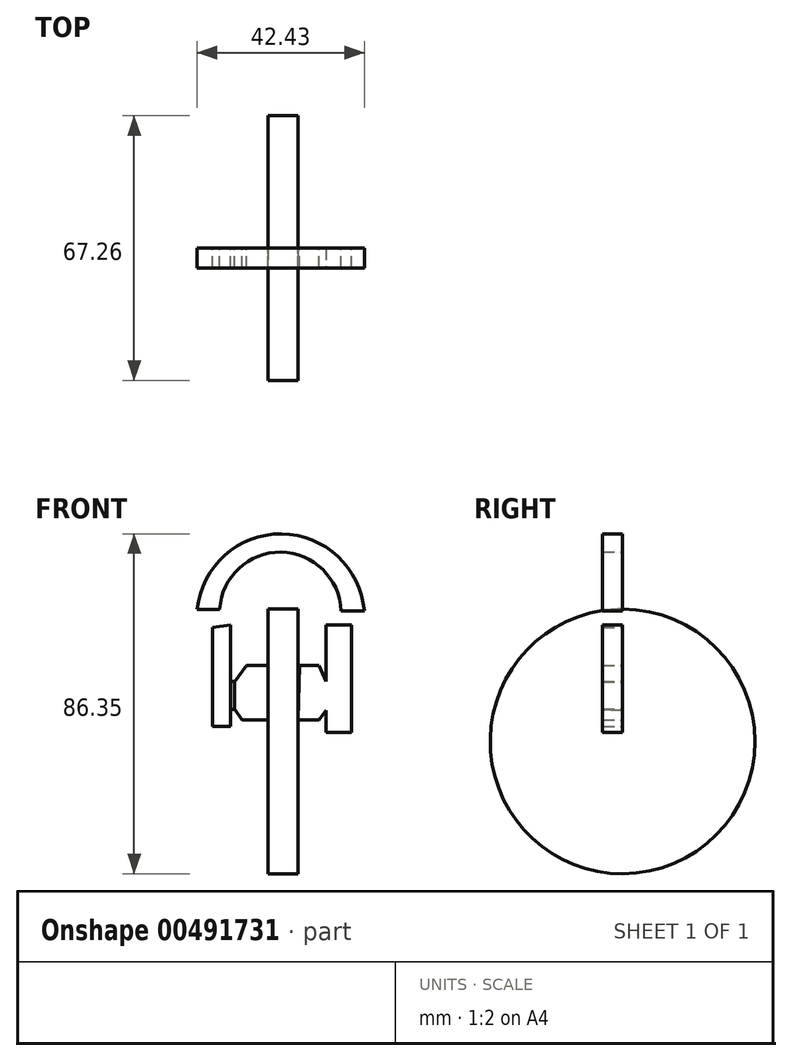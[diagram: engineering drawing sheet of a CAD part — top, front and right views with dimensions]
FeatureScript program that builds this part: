
annotation { "Feature Type Name" : "Feature", "Feature Type Description" : "" }
export const myFeature = defineFeature(function(context is Context, id is Id, definition is map)
    precondition{}
    {
        {
            var Q0;
            Q0=qCreatedBy(makeId("Right.planeOp"),FACE);
            var sketch = newSketch(context, id + "F0", { "sketchPlane" : qUnion([Q0])});
            skCircle(sketch, "E0", {"center": v(0, 0) * mm, "radius": 33.63 * mm});
            skLineSegment(sketch, "E1", {"start": v(-0.53, 0) * mm, "end": v(14.39, 30.4) * mm});
            skLineSegment(sketch, "E2", {"start": v(0.76, 0) * mm, "end": v(15.27, 29.96) * mm});
            skLineSegment(sketch, "E3", {"start": v(15.27, 29.96) * mm, "end": v(14.39, 30.4) * mm});
            skLineSegment(sketch, "E4", {"start": v(0.76, 0) * mm, "end": v(-0.53, 0) * mm});
            skSolve(sketch);
        }
        {
            var Q0;
            Q0 = qSketchRegion(id + "F0", true);
            extrude(context, id + "F1", {"entities" : qUnion([Q0]), "depth" : 7.62 * mm});
        }
        {
            var Q0;
            Q0=qCreatedBy(makeId("Front.planeOp"),FACE);
            var sketch = newSketch(context, id + "F2", { "sketchPlane" : qUnion([Q0])});
            skLineSegment(sketch, "E5", {"start": v(8.1, 19.35) * mm, "end": v(12.93, 19.35) * mm});
            skLineSegment(sketch, "E6", {"start": v(12.93, 19.35) * mm, "end": v(14.82, 15.14) * mm});
            skLineSegment(sketch, "E7", {"start": v(14.82, 15.14) * mm, "end": v(14.82, 8) * mm});
            skLineSegment(sketch, "E8", {"start": v(14.82, 8) * mm, "end": v(12.93, 5.47) * mm});
            skLineSegment(sketch, "E9", {"start": v(12.93, 5.47) * mm, "end": v(7.68, 5.47) * mm});
            skLineSegment(sketch, "E10", {"start": v(7.68, 5.47) * mm, "end": v(8.1, 19.35) * mm});
            skLineSegment(sketch, "E11", {"start": v(0, 19.35) * mm, "end": v(-5.36, 19.35) * mm});
            skLineSegment(sketch, "E12", {"start": v(-5.36, 19.35) * mm, "end": v(-8.52, 15.14) * mm});
            skLineSegment(sketch, "E13", {"start": v(-8.52, 15.14) * mm, "end": v(-8.52, 8.2) * mm});
            skLineSegment(sketch, "E14", {"start": v(-8.52, 8.2) * mm, "end": v(-6.62, 5.47) * mm});
            skLineSegment(sketch, "E15", {"start": v(-6.62, 5.47) * mm, "end": v(0, 5.47) * mm});
            skLineSegment(sketch, "E16", {"start": v(0, 5.47) * mm, "end": v(0, 19.35) * mm});
            skSolve(sketch);
        }
        {
            var Q0;
            Q0=makeQuery(id+"F2.imprint","IMPRINT",FACE,{"disambiguationData":[TD([[makeQuery(id+"F2.imprint","IMPRINT",EDGE,{"derivedFrom":sQuery(id+"F2.wireOp",EDGE,"E5")}),-1.0]])]});
            var Q1;
            Q1=makeQuery(id+"F2.imprint","IMPRINT",FACE,{"disambiguationData":[TD([[makeQuery(id+"F2.imprint","IMPRINT",EDGE,{"derivedFrom":sQuery(id+"F2.wireOp",EDGE,"E11")}),1.0]])]});
            extrude(context, id + "F3", {"entities" : qUnion([Q0, Q1]), "operationType" : NewBodyOperationType.ADD, "depth" : 5.08 * mm});
        }
        {
            var Q0;
            Q0=qCreatedBy(makeId("Front.planeOp"),FACE);
            var sketch = newSketch(context, id + "F4", { "sketchPlane" : qUnion([Q0])});
            skArc(sketch, "E17", {"start": v(24.49, 33.14) * mm, "mid": v(3.46, 52.72) * mm, "end": v(-17.94, 33.57) * mm});
            skLineSegment(sketch, "E18", {"start": v(-17.94, 33.57) * mm, "end": v(-12.24, 33.57) * mm});
            skLineSegment(sketch, "E19", {"start": v(-12.24, 33.57) * mm, "end": v(-17.94, 33.57) * mm});
            skLineSegment(sketch, "E20", {"start": v(24.49, 33.14) * mm, "end": v(18.58, 33.14) * mm});
            skLineSegment(sketch, "E21", {"start": v(18.58, 33.14) * mm, "end": v(24.49, 33.14) * mm});
            skArc(sketch, "E22", {"start": v(18.58, 33.14) * mm, "mid": v(3.37, 48.09) * mm, "end": v(-12.24, 33.57) * mm});
            skLineSegment(sketch, "E23", {"start": v(-12.24, 33.57) * mm, "end": v(-9.5, 29.56) * mm});
            skLineSegment(sketch, "E24", {"start": v(-9.5, 29.56) * mm, "end": v(-12.24, 33.57) * mm});
            skLineSegment(sketch, "E25", {"start": v(-17.94, 33.57) * mm, "end": v(-14, 28.98) * mm});
            skLineSegment(sketch, "E26", {"start": v(-14, 28.98) * mm, "end": v(-9.5, 29.56) * mm});
            skLineSegment(sketch, "E27", {"start": v(18.58, 33.14) * mm, "end": v(14.78, 29.56) * mm});
            skLineSegment(sketch, "E28", {"start": v(14.78, 29.56) * mm, "end": v(18.58, 33.14) * mm});
            skLineSegment(sketch, "E29", {"start": v(24.49, 33.14) * mm, "end": v(21.21, 29.56) * mm});
            skLineSegment(sketch, "E30", {"start": v(21.21, 29.56) * mm, "end": v(14.78, 29.56) * mm});
            skLineSegment(sketch, "E31", {"start": v(-14, 28.98) * mm, "end": v(-14, 3.8) * mm});
            skLineSegment(sketch, "E32", {"start": v(-14, 3.8) * mm, "end": v(-9.5, 3.8) * mm});
            skLineSegment(sketch, "E33", {"start": v(-9.5, 3.8) * mm, "end": v(-9.5, 29.56) * mm});
            skLineSegment(sketch, "E34", {"start": v(14.78, 29.56) * mm, "end": v(14.78, 2.32) * mm});
            skLineSegment(sketch, "E35", {"start": v(14.78, 2.32) * mm, "end": v(21.21, 2.32) * mm});
            skLineSegment(sketch, "E36", {"start": v(21.21, 2.32) * mm, "end": v(21.21, 29.56) * mm});
            skLineSegment(sketch, "E37", {"start": v(-9.5, 15.24) * mm, "end": v(-8.44, 15.24) * mm});
            skLineSegment(sketch, "E38", {"start": v(-8.44, 15.24) * mm, "end": v(-8.44, 8.14) * mm});
            skLineSegment(sketch, "E39", {"start": v(-8.44, 8.14) * mm, "end": v(-9.5, 8.14) * mm});
            skLineSegment(sketch, "E40", {"start": v(-9.5, 8.14) * mm, "end": v(-9.5, 15.24) * mm});
            skSolve(sketch);
        }
        {
            var Q0;
            Q0=makeQuery(id+"F4.imprint","IMPRINT",FACE,{"disambiguationData":[TD([[makeQuery(id+"F4.imprint","IMPRINT",EDGE,{"derivedFrom":sQuery(id+"F4.wireOp",EDGE,"E17")}),1.0]])]});
            var Q1;
            {var subQ3=sQuery(id+"F4.wireOp",EDGE,"E26");Q1=makeQuery(id+"F4.imprint","IMPRINT",FACE,{"disambiguationData":[TD([[makeQuery(id+"F4.imprint","IMPRINT",EDGE,{"derivedFrom":subQ3}),-1.0]])]});}
            var Q2;
            Q2=makeQuery(id+"F4.imprint","IMPRINT",FACE,{"disambiguationData":[TD([[makeQuery(id+"F4.imprint","IMPRINT",EDGE,{"derivedFrom":sQuery(id+"F4.wireOp",EDGE,"E19")}),1.0]])]});
            var Q3;
            Q3=makeQuery(id+"F4.imprint","IMPRINT",FACE,{"disambiguationData":[TD([[makeQuery(id+"F4.imprint","IMPRINT",EDGE,{"derivedFrom":sQuery(id+"F4.wireOp",EDGE,"E21")}),-1.0]])]});
            var Q4;
            Q4=makeQuery(id+"F4.imprint","IMPRINT",FACE,{"disambiguationData":[TD([[makeQuery(id+"F4.imprint","IMPRINT",EDGE,{"derivedFrom":sQuery(id+"F4.wireOp",EDGE,"E30")}),1.0]])]});
            extrude(context, id + "F5", {"entities" : qUnion([Q0, Q1, Q2, Q3, Q4]), "operationType" : NewBodyOperationType.ADD, "depth" : 5.08 * mm});
        }
        {
            var Q0;
            Q0=makeQuery(id+"F4.imprint","IMPRINT",FACE,{"disambiguationData":[TD([[makeQuery(id+"F4.imprint","IMPRINT",EDGE,{"derivedFrom":sQuery(id+"F4.wireOp",EDGE,"E37")}),-1.0]])]});
            extrude(context, id + "F6", {"entities" : qUnion([Q0]), "depth" : 5.08 * mm});
        }
    });
